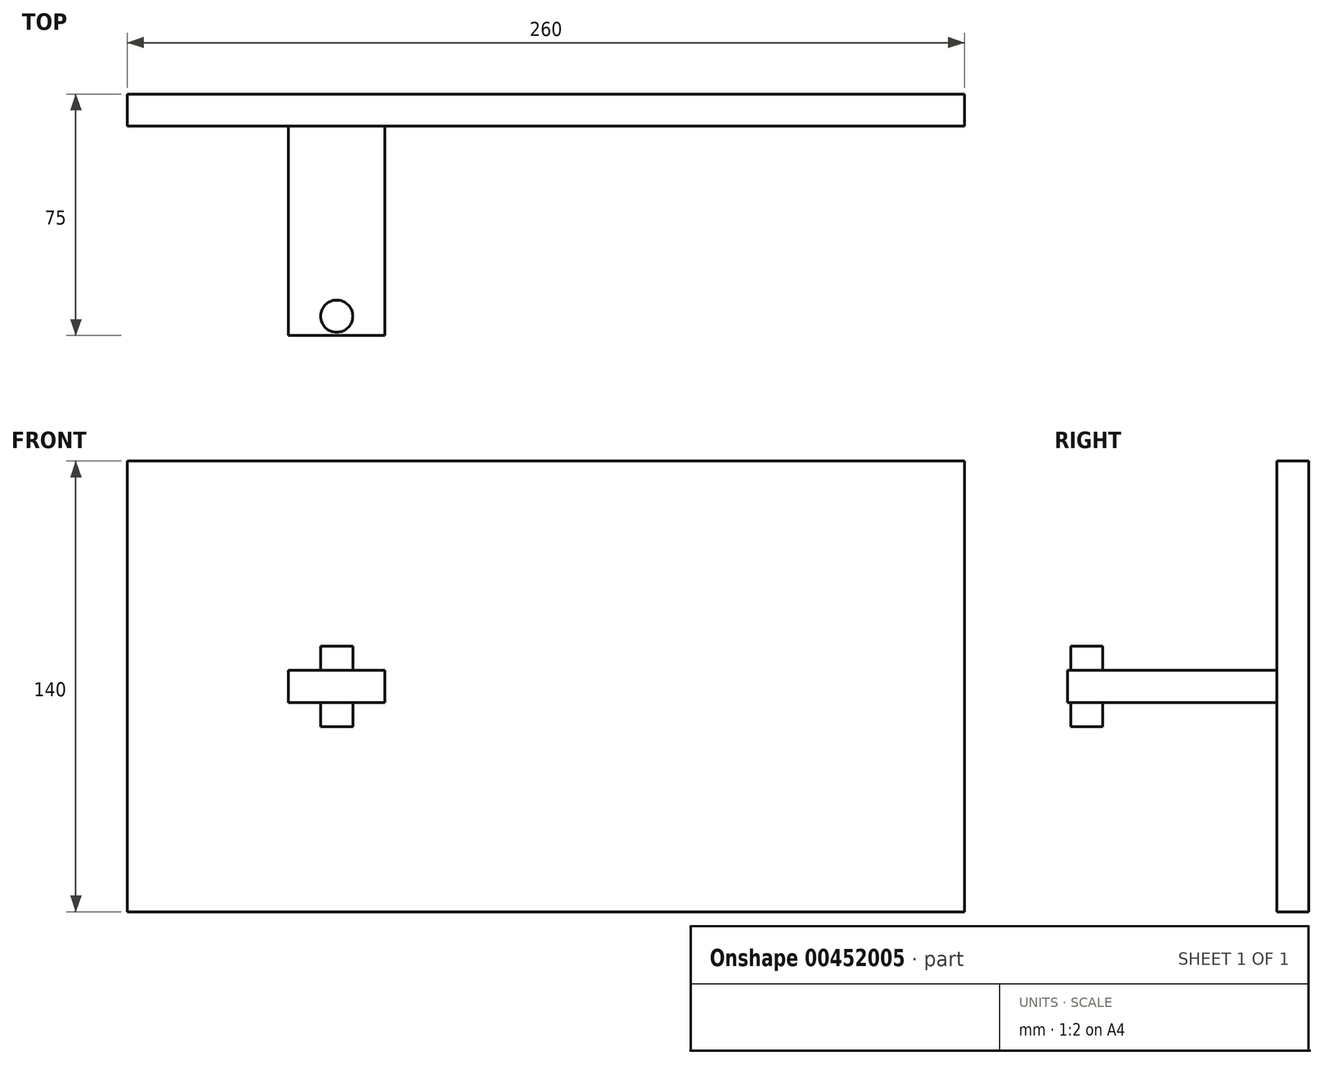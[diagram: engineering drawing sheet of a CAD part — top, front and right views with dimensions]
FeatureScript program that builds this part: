
annotation { "Feature Type Name" : "Feature", "Feature Type Description" : "" }
export const myFeature = defineFeature(function(context is Context, id is Id, definition is map)
    precondition{}
    {
        {
            var Q0;
            Q0=qCreatedBy(makeId("Front.planeOp"),FACE);
            var sketch = newSketch(context, id + "F0", { "sketchPlane" : qUnion([Q0])});
            skLineSegment(sketch, "E0.bottom", {"start": v(-130, 70) * mm, "end": v(130, 70) * mm});
            skLineSegment(sketch, "E0.top", {"start": v(-130, -70) * mm, "end": v(130, -70) * mm});
            skLineSegment(sketch, "E0.left", {"start": v(-130, 70) * mm, "end": v(-130, -70) * mm});
            skLineSegment(sketch, "E0.right", {"start": v(130, 70) * mm, "end": v(130, -70) * mm});
            skSolve(sketch);
        }
        {
            var Q0;
            Q0 = qSketchRegion(id + "F0", true);
            extrude(context, id + "F1", {"entities" : qUnion([Q0]), "endBound" : BoundingType.SYMMETRIC, "depth" : 10 * mm});
        }
        {
            var Q0;
            Q0=qCreatedBy(makeId("Top.planeOp"),FACE);
            var sketch = newSketch(context, id + "F2", { "sketchPlane" : qUnion([Q0])});
            skLineSegment(sketch, "E1.bottom", {"start": v(-80, -70) * mm, "end": v(-50, -70) * mm});
            skLineSegment(sketch, "E1.top", {"start": v(-80, -5) * mm, "end": v(-50, -5) * mm});
            skLineSegment(sketch, "E1.left", {"start": v(-80, -70) * mm, "end": v(-80, -5) * mm});
            skLineSegment(sketch, "E1.right", {"start": v(-50, -70) * mm, "end": v(-50, -5) * mm});
            skCircle(sketch, "E2", {"center": v(-65, -64) * mm, "radius": 5 * mm});
            skSolve(sketch);
        }
        {
            var Q0;
            Q0=makeQuery(id+"F2.imprint","IMPRINT",FACE,{"disambiguationData":[TD([[makeQuery(id+"F2.imprint","IMPRINT",EDGE,{"derivedFrom":sQuery(id+"F2.wireOp",EDGE,"E1.top")}),-1.0]])]});
            extrude(context, id + "F3", {"entities" : qUnion([Q0]), "endBound" : BoundingType.SYMMETRIC, "depth" : 10 * mm});
        }
        {
            var Q0;
            Q0=makeQuery(id+"F2.imprint","IMPRINT",FACE,{"disambiguationData":[TD([[makeQuery(id+"F2.imprint","IMPRINT",EDGE,{"derivedFrom":sQuery(id+"F2.wireOp",EDGE,"E2")}),1.0]])]});
            extrude(context, id + "F4", {"entities" : qUnion([Q0]), "operationType" : NewBodyOperationType.ADD, "endBound" : BoundingType.SYMMETRIC, "depth" : 25 * mm});
        }
    });
